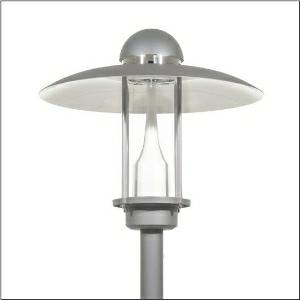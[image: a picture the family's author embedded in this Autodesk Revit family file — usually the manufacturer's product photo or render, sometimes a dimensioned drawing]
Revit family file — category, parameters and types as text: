
# Revit family: city-light_elegance_iq___st1_2a_5xa5265ef14h000022_5ab6
name_source: partatom
category: Lighting Fixtures
units: mm (PartAtom-declared; Revit-internal decimal feet)

## family parameters
Cut with Voids When Loaded = No
Host = Face
Light Source = No
Part Type = Normal
Room Calculation Point = No
Round Connector Dimension = Use Diameter
Shared = No

## types (1)
- --- (1 x LED, 1470 lm, 10.5 W, 3000K)
    Apparent Load = 11 VA
    CIE Flux Codes = 22 62 94 98 100
    Color Rendering = 70
    Color Temperature = 3000K
    Default Elevation = 1800 mm
    Description = City-Light Elegance iQ, mast luminaire, Module 540 iQ-SR, primary light control with 3 zone facetted reflector, of plastic, silver coated, highly specular, structured, primary optical cover: cover, of PMMA, transparent, light distribution: ST1.2a, light emission: direct distribution, primary light characteristic: asymmetric, installation type: post-top, LED, High Power LED, rated luminous flux: 1.470lm, luminous efficacy: 140lm/W, light colour: 730, colour temperature: 3000K, control gear: iQ Street-Remote, control: Street-Remote, Auto-Match, Temp-Guard, Lumen-Switch, Night-Set, Smart-Wire, Light-Fading, Desk-Remote (wireless, voltage-free reading and setting of iQ features in the workshop via application-optimized NFC function/RFID function), optimised constant luminous flux control (CLO 2.0), pre-setting: logarithmic dimming characteristic, mains connection: 230..240V, AC, 50/60Hz, connection cable pre-assembled, cable length: 5,5m, wiring characteristics: H07RN-F, start of lifetime: 11W, end of service life: 11W, reduction: 5W, luminaire housing, upper part, of aluminium, coated, Siteco® metallic grey (DB 702S), diameter: 750mm, height: 675mm, spigot size: d x l = 76 x 70mm (post-top) | with reducer (optional accessory) 60 x 70mm, mounting height: 3..5m, post-top mast mounting element, of diecast aluminium, coated, Siteco® metallic grey (DB 702S), Module 540 iQ-SR, traffic white (RAL 9016), equipment: standard, protection rating (complete): IP65, insulation class (complete): insulation class II (safety insulation), certification: CE, ENEC, VDE, packaging unit: 1 piece

Light Distribution: ST1.2a
    Height = 675 mm
    Lamp = 1 x LED
    Lamp Light Flux = 1470 lm
    Lamp Power = 10.5 W
    Lamp count = 1
    Length = 750 mm
    Luminous efficacy = 140 lm/W
    Manufacturer = Siteco
    ModVariant = No
    Model = 5XA5265EF14H000022
    Number of Poles = 1
    OnlyDefault = Yes
    Power Factor = 1
    Product Name = City-Light Elegance iQ | ST1.2a
    Product group = mast luminaire | pylon top
    ProductGroupID = 6100
    Protection Class = Protection class II
    Protection Degree = IP 65
    RLX_Detail_Level = 1
    RLX_Emergency_Light_Flux = 0 lm
    RLX_Emergency_Type = 0
    RLX_Emergency_Type_DB = No
    RlxData = <blob elided: 35605 chars, md5=8b51267d>
    Socket = socket
    Standby Power = 0 W
    System Light Flux = 1470 lm
    System Power = 11 W
    Type Comments = factory setting: luminous flux: 100 % | dim-lin: 254 | 419 mA
    Type Image = l_1006912.jpg
    URL = http://relux.com
    VarID = @adj_181257
    Voltage = 0 V
    Weight = 0.00 kg
    Width = 0 mm  [stored 0 ft]

note: [stored X ft] marks values corroborated as IEEE doubles in the binary element streams (Revit-internal decimal feet)

## geometry (parser evidence)
native form markers: Blend x4, Sweep x8
no freeform markers — native parametric forms only
